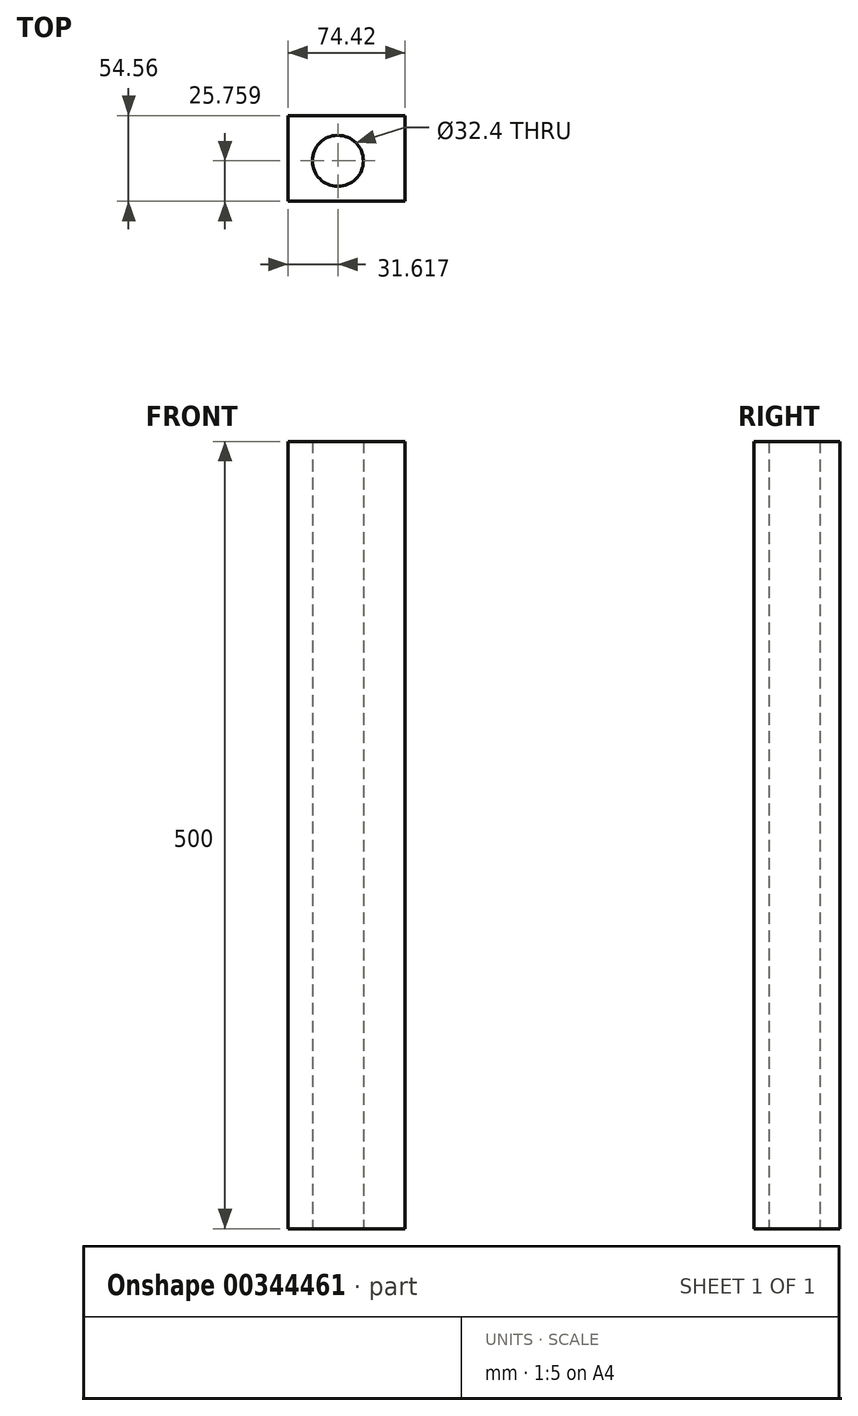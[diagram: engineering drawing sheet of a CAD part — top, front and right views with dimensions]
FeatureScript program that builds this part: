
annotation { "Feature Type Name" : "Feature", "Feature Type Description" : "" }
export const myFeature = defineFeature(function(context is Context, id is Id, definition is map)
    precondition{}
    {
        {
            var Q0;
            Q0=qCreatedBy(makeId("Top.planeOp"),FACE);
            var sketch = newSketch(context, id + "F0", { "sketchPlane" : qUnion([Q0])});
            skLineSegment(sketch, "E0.bottom", {"start": v(0, 0) * mm, "end": v(74.42, 0) * mm});
            skLineSegment(sketch, "E0.top", {"start": v(0, 54.56) * mm, "end": v(74.42, 54.56) * mm});
            skLineSegment(sketch, "E0.left", {"start": v(0, 0) * mm, "end": v(0, 54.56) * mm});
            skLineSegment(sketch, "E0.right", {"start": v(74.42, 0) * mm, "end": v(74.42, 54.56) * mm});
            skCircle(sketch, "E1", {"center": v(31.62, 25.76) * mm, "radius": 16.2 * mm});
            skSolve(sketch);
        }
        {
            var Q0;
            Q0 = qSketchRegion(id + "F0", true);
            extrude(context, id + "F1", {"entities" : qUnion([Q0]), "depth" : 500 * mm});
        }
    });
